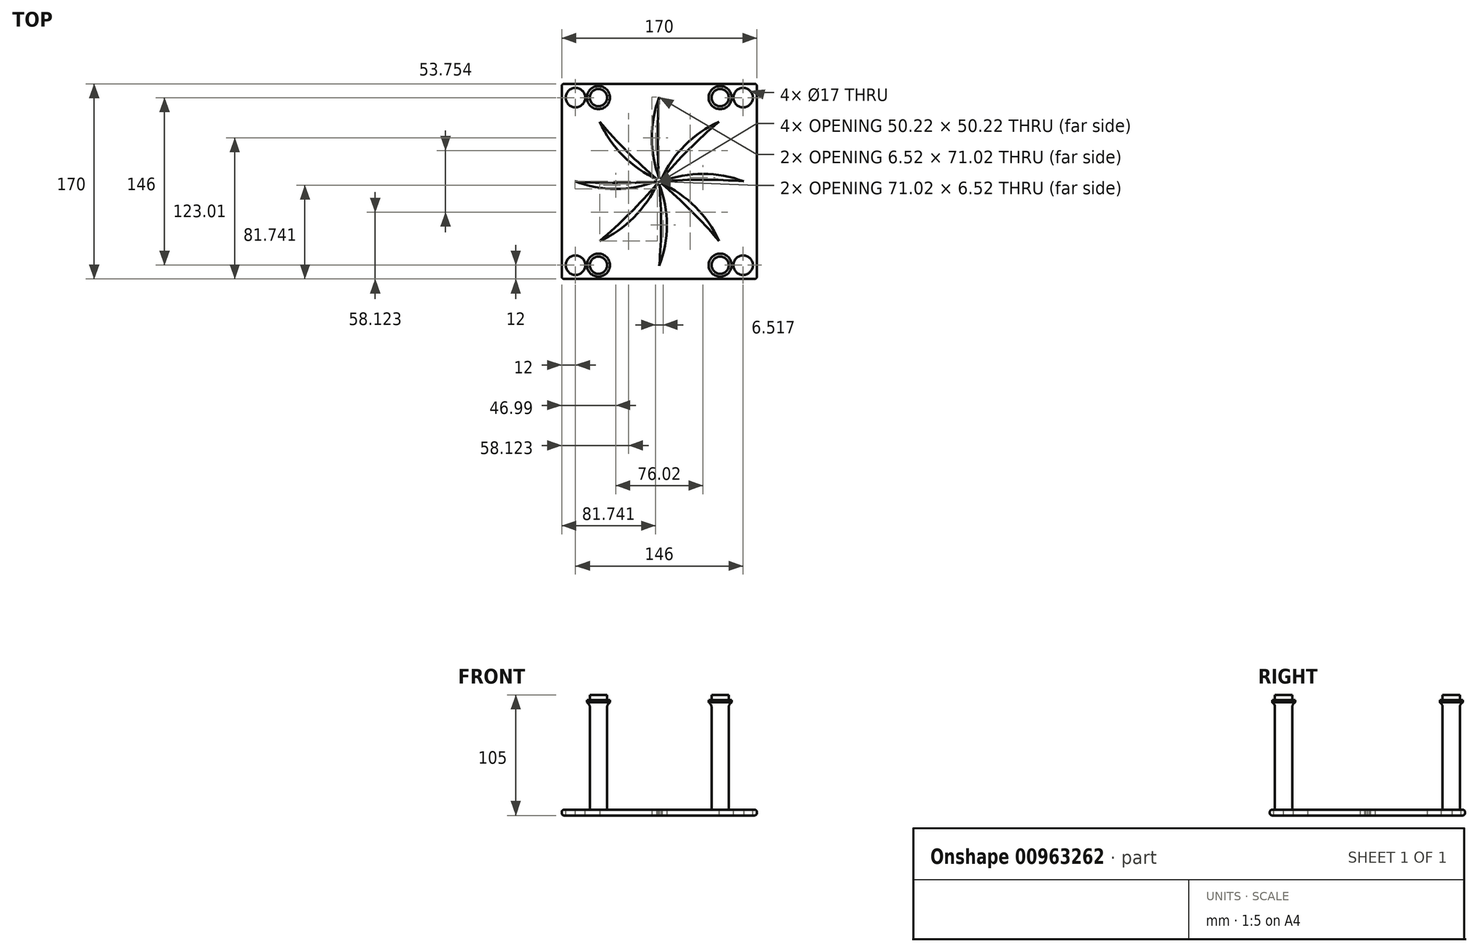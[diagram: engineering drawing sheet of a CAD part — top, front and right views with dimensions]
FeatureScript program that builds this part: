
annotation { "Feature Type Name" : "Feature", "Feature Type Description" : "" }
export const myFeature = defineFeature(function(context is Context, id is Id, definition is map)
    precondition{}
    {
        {
            var Q0;
            Q0=qCreatedBy(makeId("Top.planeOp"),FACE);
            var sketch = newSketch(context, id + "F0", { "sketchPlane" : qUnion([Q0])});
            skLineSegment(sketch, "E0.bottom", {"start": v(85, -85) * mm, "end": v(-85, -85) * mm});
            skLineSegment(sketch, "E0.top", {"start": v(85, 85) * mm, "end": v(-85, 85) * mm});
            skLineSegment(sketch, "E0.left", {"start": v(85, -85) * mm, "end": v(85, 85) * mm});
            skLineSegment(sketch, "E0.right", {"start": v(-85, -85) * mm, "end": v(-85, 85) * mm});
            skPoint(sketch, "E0.middle", {"position": v(0, 0) * mm});
            skSolve(sketch);
        }
        {
            var Q0;
            Q0=qSketchRegion(id+"F0",true);
            extrude(context, id + "F1", {"entities" : qUnion([Q0]), "depth" : 5 * mm, "offsetDistance" : 25 * mm});
        }
        {
            var Q0;
            Q0=makeQuery(id+"F1.opExtrude","CAP_EDGE",EDGE,{"disambiguationData":[OSD([sQuery(id+"F0.wireOp",EDGE,"E0.bottom")])],"isStart":false});
            var Q1;
            Q1=makeQuery(id+"F1.opExtrude","CAP_EDGE",EDGE,{"disambiguationData":[OSD([sQuery(id+"F0.wireOp",EDGE,"E0.top")])],"isStart":true});
            var Q2;
            Q2=makeQuery(id+"F1.opExtrude","CAP_EDGE",EDGE,{"disambiguationData":[OSD([sQuery(id+"F0.wireOp",EDGE,"E0.top")])],"isStart":false});
            var Q3;
            Q3=makeQuery(id+"F1.opExtrude","CAP_EDGE",EDGE,{"disambiguationData":[OSD([sQuery(id+"F0.wireOp",EDGE,"E0.left")])],"isStart":false});
            var Q4;
            Q4=makeQuery(id+"F1.opExtrude","CAP_EDGE",EDGE,{"disambiguationData":[OSD([sQuery(id+"F0.wireOp",EDGE,"E0.right")])],"isStart":true});
            var Q5;
            Q5=makeQuery(id+"F1.opExtrude","CAP_EDGE",EDGE,{"disambiguationData":[OSD([sQuery(id+"F0.wireOp",EDGE,"E0.right")])],"isStart":false});
            var Q6;
            Q6=makeQuery(id+"F1.opExtrude","SWEPT_EDGE",EDGE,{"disambiguationData":[OSD([sQuery(id+"F0.wireOp",EDGE,"E0.bottom"),sQuery(id+"F0.wireOp",EDGE,"E0.left")])]});
            var Q7;
            Q7=makeQuery(id+"F1.opExtrude","SWEPT_EDGE",EDGE,{"disambiguationData":[OSD([sQuery(id+"F0.wireOp",EDGE,"E0.bottom"),sQuery(id+"F0.wireOp",EDGE,"E0.right")])]});
            var Q8;
            Q8=makeQuery(id+"F1.opExtrude","SWEPT_EDGE",EDGE,{"disambiguationData":[OSD([sQuery(id+"F0.wireOp",EDGE,"E0.top"),sQuery(id+"F0.wireOp",EDGE,"E0.left")])]});
            var Q9;
            Q9=makeQuery(id+"F1.opExtrude","SWEPT_EDGE",EDGE,{"disambiguationData":[OSD([sQuery(id+"F0.wireOp",EDGE,"E0.top"),sQuery(id+"F0.wireOp",EDGE,"E0.right")])]});
            var Q10;
            Q10=makeQuery(id+"F1.opExtrude","CAP_EDGE",EDGE,{"disambiguationData":[OSD([sQuery(id+"F0.wireOp",EDGE,"E0.bottom")])],"isStart":true});
            var Q11;
            Q11=makeQuery(id+"F1.opExtrude","CAP_EDGE",EDGE,{"disambiguationData":[OSD([sQuery(id+"F0.wireOp",EDGE,"E0.left")])],"isStart":true});
            fillet(context, id + "F2", {"entities" : qUnion([Q0, Q1, Q2, Q3, Q4, Q5, Q6, Q7, Q8, Q9, Q10, Q11]), "radius" : 2 * mm, "tangentPropagation" : true, "allowEdgeOverflow" : false});
        }
        {
            var Q0;
            Q0=makeQuery(id+"F1.opExtrude","CAP_FACE",FACE,{"disambiguationData":[OSD([sQuery(id+"F0.wireOp",EDGE,"E0.bottom"),sQuery(id+"F0.wireOp",EDGE,"E0.top"),sQuery(id+"F0.wireOp",EDGE,"E0.left"),sQuery(id+"F0.wireOp",EDGE,"E0.right")])],"isStart":false});
            var sketch = newSketch(context, id + "F3", { "sketchPlane" : qUnion([Q0])});
            skLineSegment(sketch, "E1", {"start": v(-83, 83) * mm, "end": v(-83, 73) * mm, "construction": true});
            skLineSegment(sketch, "E2", {"start": v(-83, 73) * mm, "end": v(-73, 73) * mm, "construction": true});
            skLineSegment(sketch, "E3", {"start": v(83, 83) * mm, "end": v(83, 73) * mm, "construction": true});
            skLineSegment(sketch, "E4", {"start": v(83, 73) * mm, "end": v(73, 73) * mm, "construction": true});
            skLineSegment(sketch, "E5", {"start": v(83, -83) * mm, "end": v(83, -73) * mm, "construction": true});
            skLineSegment(sketch, "E6", {"start": v(83, -73) * mm, "end": v(73, -73) * mm, "construction": true});
            skLineSegment(sketch, "E7", {"start": v(-83, -83) * mm, "end": v(-73, -83) * mm, "construction": true});
            skLineSegment(sketch, "E8", {"start": v(-73, -83) * mm, "end": v(-73, -73) * mm, "construction": true});
            skLineSegment(sketch, "E9", {"start": v(-73, -73) * mm, "end": v(-53, -73) * mm, "construction": true});
            skLineSegment(sketch, "E10", {"start": v(73, -73) * mm, "end": v(53, -73) * mm, "construction": true});
            skLineSegment(sketch, "E11", {"start": v(73, 73) * mm, "end": v(53, 73) * mm, "construction": true});
            skLineSegment(sketch, "E12", {"start": v(-73, 73) * mm, "end": v(-53, 73) * mm, "construction": true});
            skCircle(sketch, "E13", {"center": v(-53, -73) * mm, "radius": 7.5 * mm});
            skCircle(sketch, "E14", {"center": v(53, -73) * mm, "radius": 7.5 * mm});
            skCircle(sketch, "E15", {"center": v(53, 73) * mm, "radius": 7.5 * mm});
            skCircle(sketch, "E16", {"center": v(-53, 73) * mm, "radius": 7.5 * mm});
            skSolve(sketch);
        }
        {
            var Q0;
            Q0=makeQuery(id+"F1.opExtrude","CAP_FACE",FACE,{"disambiguationData":[OSD([sQuery(id+"F0.wireOp",EDGE,"E0.bottom"),sQuery(id+"F0.wireOp",EDGE,"E0.top"),sQuery(id+"F0.wireOp",EDGE,"E0.left"),sQuery(id+"F0.wireOp",EDGE,"E0.right")])],"isStart":true});
            var sketch = newSketch(context, id + "F4", { "sketchPlane" : qUnion([Q0])});
            skCircle(sketch, "E17", {"center": v(0, 0) * mm, "radius": 25 * mm});
            skCircle(sketch, "E18", {"center": v(0, 0) * mm, "radius": 2.5 * mm});
            skArc(sketch, "E19", {"start": v(-2.5, 0) * mm, "mid": v(-38, 6.52) * mm, "end": v(-73.52, 0) * mm});
            skArc(sketch, "E20", {"start": v(-2.5, 0) * mm, "mid": v(-38, 1.52) * mm, "end": v(-73.52, 0) * mm});
            skSolve(sketch);
        }
        {
            var Q0;
            {var subQ0=sQuery(id+"F4.wireOp",EDGE,"xrmHhvh0-mqmk-Dxvq-12wP-874APo94u9yt");var subQ1=sQuery(id+"F4.wireOp",EDGE,"E17");var subQ2=makeQuery(id+"F4.imprint","INTERSECT",VERTEX,{"derivedFrom":[subQ1,subQ0]});Q0=makeQuery(id+"F4.imprint","IMPRINT",FACE,{"disambiguationData":[TD([[makeQuery(id+"F4.imprint","IMPRINT",EDGE,{"disambiguationData":[TD([[subQ2,1.0]])],"derivedFrom":subQ1}),-1.0]])]});}
            var Q1;
            {var subQ0=sQuery(id+"F4.wireOp",EDGE,"3R2oN2jj-0wEl-wqH8-dfdT-mFaKYkVUSXbc");var subQ1=sQuery(id+"F4.wireOp",EDGE,"E17");var subQ2=makeQuery(id+"F4.imprint","INTERSECT",VERTEX,{"derivedFrom":[subQ1,subQ0]});Q1=makeQuery(id+"F4.imprint","IMPRINT",FACE,{"disambiguationData":[TD([[makeQuery(id+"F4.imprint","IMPRINT",EDGE,{"disambiguationData":[TD([[subQ2,-1.0]])],"derivedFrom":subQ1}),1.0]])]});}
            extrude(context, id + "F5", {"entities" : qUnion([Q0, Q1]), "depth" : 25 * mm, "offsetDistance" : 25 * mm});
        }
        {
            var Q0;
            Q0=makeQuery(id+"F5.opExtrude","SWEPT_BODY",BODY,{"disambiguationData":[OSD([sQuery(id+"F4.wireOp",EDGE,"E19"),sQuery(id+"F4.wireOp",EDGE,"E20")])]});
            var Q1;
            Q1=sQuery(id+"F4.wireOp",EDGE,"E17");
            circularPattern(context, id + "F6", {"entities" : qUnion([Q0]), "axis" : qUnion([Q1]), "angle" : 360 * degree, "instanceCount" : 8, "equalSpace" : true});
        }
        {
            var Q0;
            Q0=makeQuery(id+"F6.opPattern","COPY",FACE,{"derivedFrom":makeQuery(id+"F5.opExtrude","CAP_FACE",FACE,{"disambiguationData":[OSD([sQuery(id+"F4.wireOp",EDGE,"E19"),sQuery(id+"F4.wireOp",EDGE,"E20")])],"isStart":false}),"instanceName":"6"});
            var Q1;
            Q1=makeQuery(id+"F6.opPattern","COPY",FACE,{"derivedFrom":makeQuery(id+"F5.opExtrude","CAP_FACE",FACE,{"disambiguationData":[OSD([sQuery(id+"F4.wireOp",EDGE,"E19"),sQuery(id+"F4.wireOp",EDGE,"E20")])],"isStart":false}),"instanceName":"7"});
            var Q2;
            Q2=makeQuery(id+"F6.opPattern","COPY",FACE,{"derivedFrom":makeQuery(id+"F5.opExtrude","CAP_FACE",FACE,{"disambiguationData":[OSD([sQuery(id+"F4.wireOp",EDGE,"E19"),sQuery(id+"F4.wireOp",EDGE,"E20")])],"isStart":false}),"instanceName":"5"});
            var Q3;
            Q3=makeQuery(id+"F6.opPattern","COPY",FACE,{"derivedFrom":makeQuery(id+"F5.opExtrude","CAP_FACE",FACE,{"disambiguationData":[OSD([sQuery(id+"F4.wireOp",EDGE,"E19"),sQuery(id+"F4.wireOp",EDGE,"E20")])],"isStart":false}),"instanceName":"4"});
            var Q4;
            Q4=makeQuery(id+"F6.opPattern","COPY",FACE,{"derivedFrom":makeQuery(id+"F5.opExtrude","CAP_FACE",FACE,{"disambiguationData":[OSD([sQuery(id+"F4.wireOp",EDGE,"E19"),sQuery(id+"F4.wireOp",EDGE,"E20")])],"isStart":false}),"instanceName":"3"});
            var Q5;
            Q5=makeQuery(id+"F6.opPattern","COPY",FACE,{"derivedFrom":makeQuery(id+"F5.opExtrude","CAP_FACE",FACE,{"disambiguationData":[OSD([sQuery(id+"F4.wireOp",EDGE,"E19"),sQuery(id+"F4.wireOp",EDGE,"E20")])],"isStart":false}),"instanceName":"2"});
            var Q6;
            Q6=makeQuery(id+"F6.opPattern","COPY",FACE,{"derivedFrom":makeQuery(id+"F5.opExtrude","CAP_FACE",FACE,{"disambiguationData":[OSD([sQuery(id+"F4.wireOp",EDGE,"E19"),sQuery(id+"F4.wireOp",EDGE,"E20")])],"isStart":false}),"instanceName":"1"});
            var Q7;
            Q7=makeQuery(id+"F5.opExtrude","CAP_FACE",FACE,{"disambiguationData":[OSD([sQuery(id+"F4.wireOp",EDGE,"E19"),sQuery(id+"F4.wireOp",EDGE,"E20")])],"isStart":false});
            extrude(context, id + "F7", {"entities" : qUnion([Q0, Q1, Q2, Q3, Q4, Q5, Q6, Q7]), "operationType" : NewBodyOperationType.REMOVE, "oppositeDirection" : true, "depth" : 50 * mm, "offsetDistance" : 25 * mm});
        }
        {
            var Q0;
            Q0=sQuery(id+"F3.wireOp",VERTEX,"E8.end");
            var Q1;
            Q1=sQuery(id+"F3.wireOp",VERTEX,"E6.end");
            var Q2;
            Q2=sQuery(id+"F3.wireOp",VERTEX,"E4.end");
            var Q3;
            Q3=sQuery(id+"F3.wireOp",VERTEX,"E2.end");
            var Q4;
            Q4=makeQuery(id+"F1.opExtrude","SWEPT_BODY",BODY,{"disambiguationData":[OSD([sQuery(id+"F0.wireOp",EDGE,"E0.bottom"),sQuery(id+"F0.wireOp",EDGE,"E0.top"),sQuery(id+"F0.wireOp",EDGE,"E0.left"),sQuery(id+"F0.wireOp",EDGE,"E0.right")])]});
            hole(context, id + "F8", {"style" : HoleStyle.SIMPLE, "endStyle" : HoleEndStyle.THROUGH, "holeDiameter" : 17 * mm, "majorDiameter" : 5 * mm, "isTappedThrough" : true, "tappedDepth" : 12 * mm, "tapClearance" : 3, "locations" : qUnion([Q0, Q1, Q2, Q3]), "scope" : qUnion([Q4])});
        }
        {
            var Q0;
            Q0 = qSketchRegion(id + "F3", true);
            extrude(context, id + "F9", {"entities" : qUnion([Q0]), "operationType" : NewBodyOperationType.ADD, "depth" : 95.5 * mm, "offsetDistance" : 25 * mm});
        }
        {
            var Q0;
            Q0=makeQuery(id+"F9.opExtrude","CAP_FACE",FACE,{"disambiguationData":[OSD([sQuery(id+"F3.wireOp",EDGE,"E16")])],"isStart":false});
            var sketch = newSketch(context, id + "F10", { "sketchPlane" : qUnion([Q0])});
            skCircle(sketch, "E21", {"center": v(-53, 73) * mm, "radius": 10 * mm});
            skSolve(sketch);
        }
        {
            var Q0;
            Q0=makeQuery(id+"F9.opExtrude","CAP_FACE",FACE,{"disambiguationData":[OSD([sQuery(id+"F3.wireOp",EDGE,"E15")])],"isStart":false});
            var sketch = newSketch(context, id + "F11", { "sketchPlane" : qUnion([Q0])});
            skCircle(sketch, "E22", {"center": v(53, 73) * mm, "radius": 10 * mm});
            skSolve(sketch);
        }
        {
            var Q0;
            Q0=makeQuery(id+"F9.opExtrude","CAP_FACE",FACE,{"disambiguationData":[OSD([sQuery(id+"F3.wireOp",EDGE,"E14")])],"isStart":false});
            var sketch = newSketch(context, id + "F12", { "sketchPlane" : qUnion([Q0])});
            skCircle(sketch, "E23", {"center": v(53, -73) * mm, "radius": 10 * mm});
            skSolve(sketch);
        }
        {
            var Q0;
            Q0=makeQuery(id+"F9.opExtrude","CAP_FACE",FACE,{"disambiguationData":[OSD([sQuery(id+"F3.wireOp",EDGE,"E13")])],"isStart":false});
            var sketch = newSketch(context, id + "F13", { "sketchPlane" : qUnion([Q0])});
            skCircle(sketch, "E24", {"center": v(-53, -73) * mm, "radius": 10 * mm});
            skSolve(sketch);
        }
        {
            var Q0;
            Q0=makeQuery(id+"F10.imprint","IMPRINT",FACE,{"disambiguationData":[TD([[makeQuery(id+"F10.imprint","IMPRINT",EDGE,{"derivedFrom":makeQuery(id+"F9.opExtrude","CAP_EDGE",EDGE,{"disambiguationData":[OSD([sQuery(id+"F3.wireOp",EDGE,"E16")])],"isStart":false})}),1.0]])]});
            var Q1;
            Q1=makeQuery(id+"F11.imprint","IMPRINT",FACE,{"disambiguationData":[TD([[makeQuery(id+"F11.imprint","IMPRINT",EDGE,{"derivedFrom":makeQuery(id+"F9.opExtrude","CAP_EDGE",EDGE,{"disambiguationData":[OSD([sQuery(id+"F3.wireOp",EDGE,"E15")])],"isStart":false})}),1.0]])]});
            var Q2;
            Q2=makeQuery(id+"F12.imprint","IMPRINT",FACE,{"disambiguationData":[TD([[makeQuery(id+"F12.imprint","IMPRINT",EDGE,{"derivedFrom":makeQuery(id+"F9.opExtrude","CAP_EDGE",EDGE,{"disambiguationData":[OSD([sQuery(id+"F3.wireOp",EDGE,"E14")])],"isStart":false})}),1.0]])]});
            var Q3;
            Q3=makeQuery(id+"F13.imprint","IMPRINT",FACE,{"disambiguationData":[TD([[makeQuery(id+"F13.imprint","IMPRINT",EDGE,{"derivedFrom":makeQuery(id+"F9.opExtrude","CAP_EDGE",EDGE,{"disambiguationData":[OSD([sQuery(id+"F3.wireOp",EDGE,"E13")])],"isStart":false})}),1.0]])]});
            extrude(context, id + "F14", {"entities" : qUnion([Q0, Q1, Q2, Q3]), "operationType" : NewBodyOperationType.ADD, "depth" : 4.5 * mm, "offsetDistance" : 25 * mm});
        }
        {
            var Q0;
            Q0=makeQuery(id+"F10.imprint","IMPRINT",FACE,{"disambiguationData":[TD([[makeQuery(id+"F10.imprint","IMPRINT",EDGE,{"derivedFrom":sQuery(id+"F10.wireOp",EDGE,"E21")}),1.0]])]});
            var Q1;
            Q1=makeQuery(id+"F11.imprint","IMPRINT",FACE,{"disambiguationData":[TD([[makeQuery(id+"F11.imprint","IMPRINT",EDGE,{"derivedFrom":sQuery(id+"F11.wireOp",EDGE,"E22")}),1.0]])]});
            var Q2;
            Q2=makeQuery(id+"F12.imprint","IMPRINT",FACE,{"disambiguationData":[TD([[makeQuery(id+"F12.imprint","IMPRINT",EDGE,{"derivedFrom":sQuery(id+"F12.wireOp",EDGE,"E23")}),1.0]])]});
            var Q3;
            Q3=makeQuery(id+"F13.imprint","IMPRINT",FACE,{"disambiguationData":[TD([[makeQuery(id+"F13.imprint","IMPRINT",EDGE,{"derivedFrom":sQuery(id+"F13.wireOp",EDGE,"E24")}),1.0]])]});
            extrude(context, id + "F15", {"entities" : qUnion([Q0, Q1, Q2, Q3]), "operationType" : NewBodyOperationType.ADD, "oppositeDirection" : true, "depth" : 2 * mm, "offsetDistance" : 25 * mm});
        }
        {
            var Q0;
            Q0=makeQuery(id+"F15.opExtrude","CAP_EDGE",EDGE,{"disambiguationData":[OSD([sQuery(id+"F3.wireOp",EDGE,"E13")])],"isStart":false});
            var Q1;
            Q1=makeQuery(id+"F15.opExtrude","CAP_EDGE",EDGE,{"disambiguationData":[OSD([sQuery(id+"F3.wireOp",EDGE,"E14")])],"isStart":false});
            var Q2;
            Q2=makeQuery(id+"F15.opExtrude","CAP_EDGE",EDGE,{"disambiguationData":[OSD([sQuery(id+"F3.wireOp",EDGE,"E15")])],"isStart":false});
            var Q3;
            Q3=makeQuery(id+"F15.opExtrude","CAP_EDGE",EDGE,{"disambiguationData":[OSD([sQuery(id+"F3.wireOp",EDGE,"E16")])],"isStart":false});
            fillet(context, id + "F16", {"entities" : qUnion([Q0, Q1, Q2, Q3]), "radius" : 5 * mm, "tangentPropagation" : true, "allowEdgeOverflow" : false});
        }
    });
